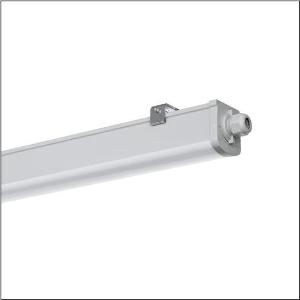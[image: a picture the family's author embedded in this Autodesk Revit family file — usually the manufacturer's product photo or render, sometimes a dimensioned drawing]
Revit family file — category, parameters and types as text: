
# Revit family: monsun_r__31_51fa207p430b_b845
name_source: partatom
category: Lighting Fixtures
units: mm (PartAtom-declared; Revit-internal decimal feet)

## family parameters
Cut with Voids When Loaded = No
Host = Face
Light Source = No
Part Type = Normal
Room Calculation Point = No
Round Connector Dimension = Use Diameter
Shared = No

## types (1)
- Monsun® 31 (1 x LED, 3800 lm, 28 W, 4000K)
    Apparent Load = 28 VA
    CIE Flux Codes = 42 72 91 92 100
    Color Rendering = 80
    Color Temperature = 4000K
    Default Elevation = 1800 mm
    Description = Monsun® 31, damp-proof luminaire, primary optical cover: diffuser, of PC, frosted, light emission: direct distribution, primary light characteristic: symmetric, installation type: surface-mounted, LED, rated luminous flux: 3.800lm, luminous efficacy: 136lm/W, light colour: 840, colour temperature: 4000K, control gear: ECG, with terminal, 3+1-pole, max. 2.5mm², through-wiring: 3x 2.5mm² + 1x 1.5mm², mains connection: 220..240V, AC, 50/60Hz, rated input power: 28W, housing, luminaire housing, of PC, light grey (RAL 7035), length: 1.458mm, width: 68mm, height: 76mm, protection rating (complete): IP66, insulation class (complete): insulation class II (safety insulation), certification: CE, ENEC, UKCA, protection symbol: D, impact resistance: IK08, permissible operating ambient temperature: -20..+40°C, corresponds to IFS (International Featured Standards) requirements for safety and quality in the food industry, contact your sales advisor before using the luminaires in applications with unclear chemical exposure, large temperature fluctuations or condensation-forming humidity, packaging unit: 1 piece
    Height = 77 mm
    Lamp = 1 x LED
    Lamp Light Flux = 3800 lm
    Lamp Power = 28 W
    Lamp count = 1
    Length = 1518 mm
    Luminous efficacy = 136 lm/W
    Manufacturer = Siteco
    ModVariant = No
    Model = 51FA207P430B
    Mounting Place = Ceiling
    Mounting Type = Surface mounted
    Number of Poles = 1
    OnlyDefault = Yes
    Power Factor = 1
    Product Name = Monsun® 31
    Product group = damp-proof luminaire
    ProductGroupID = 300
    Protection Class = Protection class II
    Protection Degree = IP 66
    RLX_Detail_Level = 1
    RLX_Emergency_Light_Flux = 0 lm
    RLX_Emergency_Type = 0
    RLX_Emergency_Type_DB = No
    RlxData = <blob elided: 33177 chars, md5=70563e1f>
    Socket = socket
    Standby Power = 0 W
    System Light Flux = 3800 lm
    System Power = 28 W
    Type Comments = Product without accessories
    Type Image = l_1006174.jpg
    URL = http://relux.com
    VarID = ---
    Voltage = 0 V
    Weight = 0.00 kg
    Width = 69 mm

## geometry (parser evidence)
native form markers: Blend x4, Sweep x14
no freeform markers — native parametric forms only
